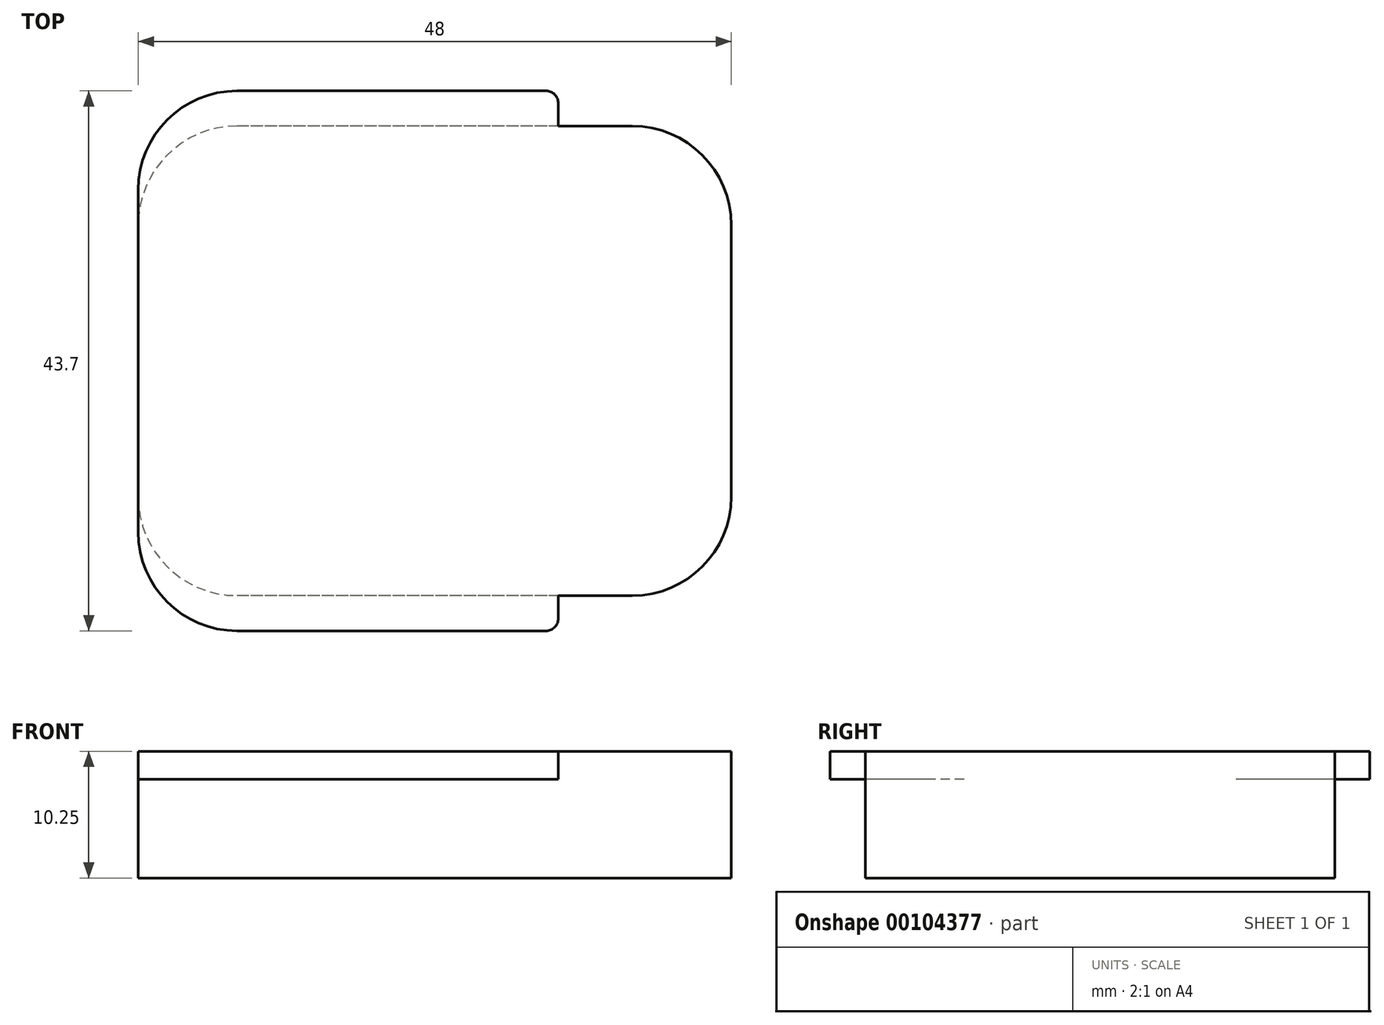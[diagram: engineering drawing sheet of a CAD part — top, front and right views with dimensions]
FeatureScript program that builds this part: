
annotation { "Feature Type Name" : "Feature", "Feature Type Description" : "" }
export const myFeature = defineFeature(function(context is Context, id is Id, definition is map)
    precondition{}
    {
        {
            var Q0;
            Q0=qCreatedBy(makeId("Top.planeOp"),FACE);
            var sketch = newSketch(context, id + "F0", { "sketchPlane" : qUnion([Q0])});
            skLineSegment(sketch, "E0.bottom", {"start": v(16, -19) * mm, "end": v(-16, -19) * mm});
            skLineSegment(sketch, "E0.top", {"start": v(16, 19) * mm, "end": v(-16, 19) * mm});
            skLineSegment(sketch, "E0.left", {"start": v(24, -11) * mm, "end": v(24, 11) * mm});
            skLineSegment(sketch, "E0.right", {"start": v(-24, -11) * mm, "end": v(-24, 11) * mm});
            skPoint(sketch, "E0.middle", {"position": v(0, 0) * mm});
            skPoint(sketch, "E1.visualSharp", {"position": v(24, -19) * mm});
            skArc(sketch, "E1.filletArc", {"start": v(16, -19) * mm, "mid": v(21.66, -16.66) * mm, "end": v(24, -11) * mm});
            skPoint(sketch, "E2.visualSharp", {"position": v(24, 19) * mm});
            skArc(sketch, "E2.filletArc", {"start": v(24, 11) * mm, "mid": v(21.66, 16.66) * mm, "end": v(16, 19) * mm});
            skPoint(sketch, "E3.visualSharp", {"position": v(-24, -19) * mm});
            skArc(sketch, "E3.filletArc", {"start": v(-24, -11) * mm, "mid": v(-21.66, -16.66) * mm, "end": v(-16, -19) * mm});
            skPoint(sketch, "E4.visualSharp", {"position": v(-24, 19) * mm});
            skArc(sketch, "E4.filletArc", {"start": v(-16, 19) * mm, "mid": v(-21.66, 16.66) * mm, "end": v(-24, 11) * mm});
            skSolve(sketch);
        }
        {
            var Q0;
            Q0 = qSketchRegion(id + "F0", true);
            extrude(context, id + "F1", {"entities" : qUnion([Q0]), "depth" : 10.25 * mm});
        }
        {
            var Q0;
            Q0=makeQuery(id+"F1.opExtrude","CAP_FACE",FACE,{"disambiguationData":[OSD([sQuery(id+"F0.wireOp",EDGE,"E0.bottom"),sQuery(id+"F0.wireOp",EDGE,"E0.top"),sQuery(id+"F0.wireOp",EDGE,"E0.left"),sQuery(id+"F0.wireOp",EDGE,"E0.right"),sQuery(id+"F0.wireOp",EDGE,"E1.filletArc"),sQuery(id+"F0.wireOp",EDGE,"E2.filletArc"),sQuery(id+"F0.wireOp",EDGE,"E3.filletArc"),sQuery(id+"F0.wireOp",EDGE,"E4.filletArc")])],"isStart":false});
            var sketch = newSketch(context, id + "F2", { "sketchPlane" : qUnion([Q0])});
            skLineSegment(sketch, "E5.bottom", {"start": v(-16, 21.85) * mm, "end": v(9, 21.85) * mm});
            skLineSegment(sketch, "E5.top", {"start": v(-16, -21.85) * mm, "end": v(9, -21.85) * mm});
            skLineSegment(sketch, "E5.left", {"start": v(-24, 13.85) * mm, "end": v(-24, -13.85) * mm});
            skLineSegment(sketch, "E5.right", {"start": v(10, 20.85) * mm, "end": v(10, -20.85) * mm});
            skPoint(sketch, "E6.visualSharp", {"position": v(-24, 21.85) * mm});
            skArc(sketch, "E6.filletArc", {"start": v(-16, 21.85) * mm, "mid": v(-21.66, 19.5) * mm, "end": v(-24, 13.85) * mm});
            skPoint(sketch, "E7.visualSharp", {"position": v(-24, -21.85) * mm});
            skArc(sketch, "E7.filletArc", {"start": v(-24, -13.85) * mm, "mid": v(-21.66, -19.5) * mm, "end": v(-16, -21.85) * mm});
            skPoint(sketch, "E8.visualSharp", {"position": v(10, 21.85) * mm});
            skArc(sketch, "E8.filletArc", {"start": v(10, 20.85) * mm, "mid": v(9.7, 21.56) * mm, "end": v(9, 21.85) * mm});
            skPoint(sketch, "E9.visualSharp", {"position": v(10, -21.85) * mm});
            skArc(sketch, "E9.filletArc", {"start": v(9, -21.85) * mm, "mid": v(9.7, -21.56) * mm, "end": v(10, -20.85) * mm});
            skSolve(sketch);
        }
        {
            var Q0;
            Q0=makeQuery(id+"F2.imprint","IMPRINT",FACE,{"disambiguationData":[TD([[makeQuery(id+"F2.imprint","IMPRINT",EDGE,{"derivedFrom":sQuery(id+"F2.wireOp",EDGE,"E5.bottom")}),-1.0]])]});
            var Q1;
            Q1=makeQuery(id+"F2.imprint","IMPRINT",FACE,{"disambiguationData":[TD([[makeQuery(id+"F2.imprint","IMPRINT",EDGE,{"derivedFrom":sQuery(id+"F2.wireOp",EDGE,"E5.top")}),1.0]])]});
            var Q2;
            {var subQ0=makeQuery(id+"F1.opExtrude","CAP_EDGE",EDGE,{"disambiguationData":[OSD([sQuery(id+"F0.wireOp",EDGE,"E3.filletArc")])],"isStart":false});Q2=makeQuery(id+"F2.imprint","IMPRINT",FACE,{"disambiguationData":[TD([[makeQuery(id+"F2.imprint","IMPRINT",EDGE,{"derivedFrom":subQ0}),1.0]])]});}
            extrude(context, id + "F3", {"entities" : qUnion([Q0, Q1, Q2]), "operationType" : NewBodyOperationType.ADD, "oppositeDirection" : true, "depth" : 2.25 * mm});
        }
    });
